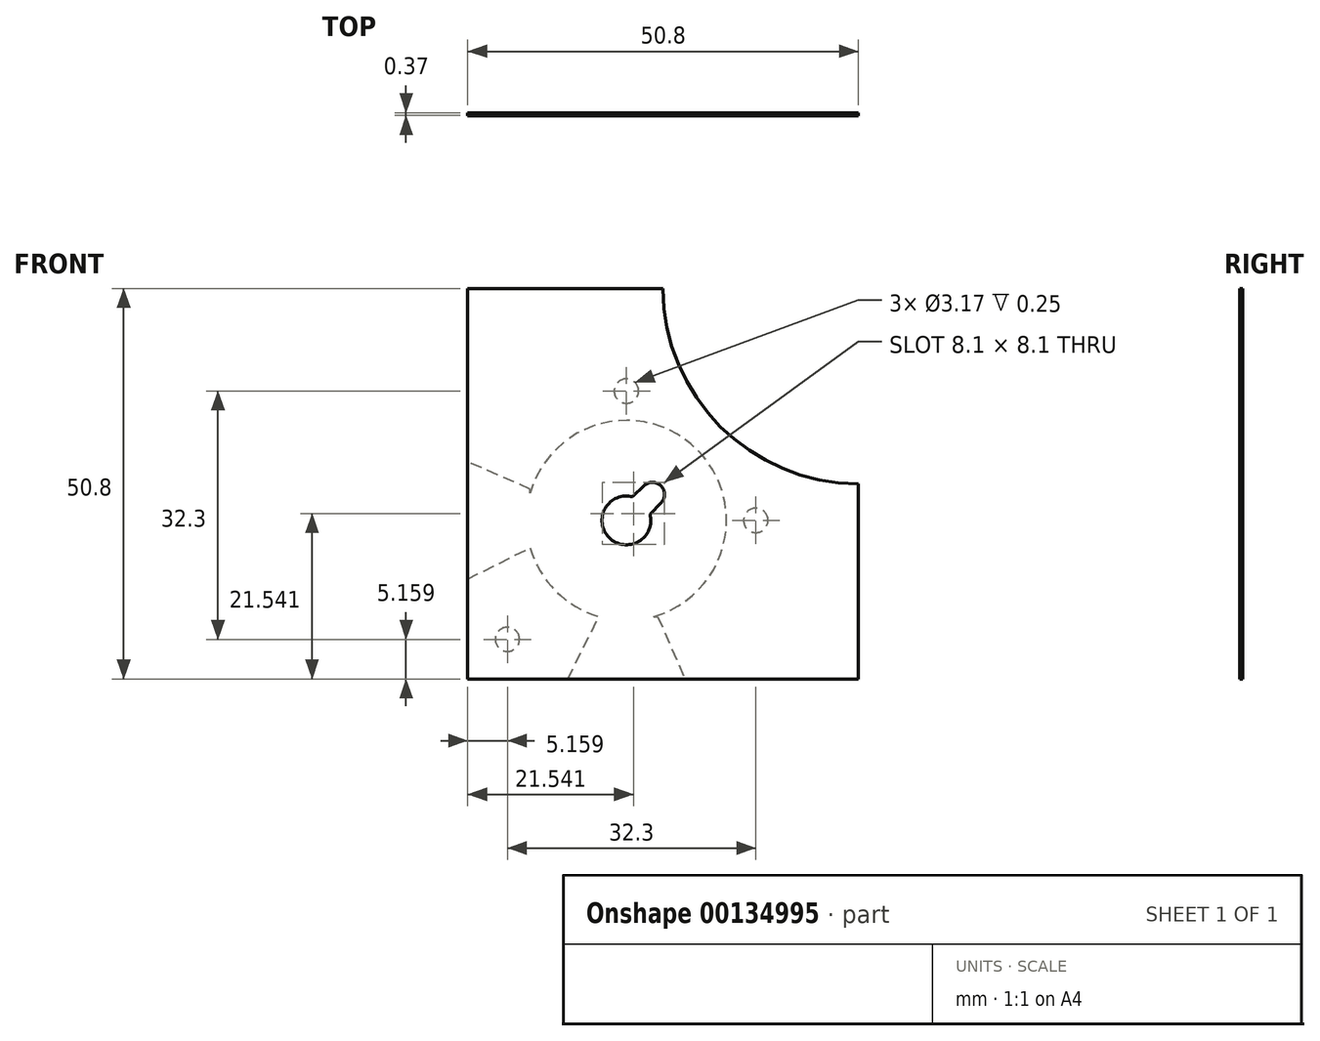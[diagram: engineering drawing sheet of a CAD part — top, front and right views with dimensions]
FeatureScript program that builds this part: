
annotation { "Feature Type Name" : "Feature", "Feature Type Description" : "" }
export const myFeature = defineFeature(function(context is Context, id is Id, definition is map)
    precondition{}
    {
        {
            assignVariable(context, id + "F0", {"name" : "Thickness", "anyValue" : .375});
        }
        {
            var Q0;
            Q0=qCreatedBy(makeId("Front.planeOp"),FACE);
            var sketch = newSketch(context, id + "F1", { "sketchPlane" : qUnion([Q0])});
            skLineSegment(sketch, "E0.bottom", {"start": v(0, 0) * mm, "end": v(50.8, 0) * mm});
            skLineSegment(sketch, "E0.top", {"start": v(0, 50.8) * mm, "end": v(25.4, 50.8) * mm});
            skLineSegment(sketch, "E0.left", {"start": v(0, 0) * mm, "end": v(0, 50.8) * mm});
            skLineSegment(sketch, "E0.right", {"start": v(50.8, 0) * mm, "end": v(50.8, 25.4) * mm});
            skPoint(sketch, "E1.orphan", {"position": v(50.8, 50.8) * mm});
            skArc(sketch, "E2", {"start": v(25.4, 50.8) * mm, "mid": v(32.84, 32.84) * mm, "end": v(50.8, 25.4) * mm});
            skSolve(sketch);
        }
        {
            var Q0;
            Q0=qCreatedBy(makeId("Front.planeOp"),FACE);
            var sketch = newSketch(context, id + "F2", { "sketchPlane" : qUnion([Q0])});
            skCircle(sketch, "E3", {"center": v(10.32, 10.32) * mm, "radius": 3.18 * mm});
            skCircle(sketch, "E4.0.1.0", {"center": v(10.32, 30.96) * mm, "radius": 3.18 * mm});
            skCircle(sketch, "E4.1.0.0", {"center": v(30.96, 10.32) * mm, "radius": 3.18 * mm});
            skLineSegment(sketch, "E4.direction1", {"start": v(10.32, 10.32) * mm, "end": v(30.96, 10.32) * mm, "construction": true});
            skLineSegment(sketch, "E4.direction2", {"start": v(10.32, 10.32) * mm, "end": v(10.32, 30.96) * mm, "construction": true});
            skSolve(sketch);
        }
        {
            var Q0;
            Q0=qCreatedBy(makeId("Front.planeOp"),FACE);
            var sketch = newSketch(context, id + "F3", { "sketchPlane" : qUnion([Q0])});
            skCircle(sketch, "E5", {"center": v(20.64, 20.64) * mm, "radius": 13 * mm});
            skSolve(sketch);
        }
        {
            var Q0;
            Q0=qCreatedBy(makeId("Front.planeOp"),FACE);
            var sketch = newSketch(context, id + "F4", { "sketchPlane" : qUnion([Q0])});
            skCircle(sketch, "E6", {"center": v(20.64, 3.82) * mm, "radius": 1.59 * mm, "construction": true});
            skLineSegment(sketch, "E7", {"start": v(20.64, 0) * mm, "end": v(20.64, 7.63) * mm, "construction": true});
            skLineSegment(sketch, "E8", {"start": v(0, 0) * mm, "end": v(10.32, 10.32) * mm, "construction": true});
            skLineSegment(sketch, "E9", {"start": v(10.32, 30.96) * mm, "end": v(30.96, 10.32) * mm, "construction": true});
            skCircle(sketch, "E10.MirrorC", {"center": v(37.46, 20.64) * mm, "radius": 1.59 * mm});
            skCircle(sketch, "E11.MirrorC", {"center": v(3.82, 20.64) * mm, "radius": 1.59 * mm, "construction": true});
            skCircle(sketch, "E12.MirrorC", {"center": v(20.64, 37.46) * mm, "radius": 1.59 * mm});
            skCircle(sketch, "E13", {"center": v(5.16, 5.16) * mm, "radius": 1.59 * mm});
            skSolve(sketch);
        }
        {
            var Q0;
            Q0=qCreatedBy(makeId("Front.planeOp"),FACE);
            var sketch = newSketch(context, id + "F5", { "sketchPlane" : qUnion([Q0])});
            skCircle(sketch, "E14", {"center": v(15.48, 15.48) * mm, "radius": 1.65 * mm});
            skLineSegment(sketch, "E15", {"start": v(10.32, 10.32) * mm, "end": v(20.64, 20.64) * mm, "construction": true});
            skSolve(sketch);
        }
        {
            var Q0;
            Q0=makeQuery(id+"F1.imprint","IMPRINT",FACE,{"disambiguationData":[TD([[makeQuery(id+"F1.imprint","IMPRINT",EDGE,{"derivedFrom":sQuery(id+"F1.wireOp",EDGE,"E0.bottom")}),1.0]])]});
            var sketch = newSketch(context, id + "F6", { "sketchPlane" : qUnion([Q0])});
            skLineSegment(sketch, "E16", {"start": v(20.64, 20.64) * mm, "end": v(33.64, 20.64) * mm, "construction": true});
            skLineSegment(sketch, "E17", {"start": v(27.14, 20.64) * mm, "end": v(16.82, 0) * mm, "construction": true});
            skLineSegment(sketch, "E18", {"start": v(20.64, 0) * mm, "end": v(13, 0) * mm, "construction": true});
            skLineSegment(sketch, "E19", {"start": v(13, 0) * mm, "end": v(23.32, 20.64) * mm, "construction": true});
            skLineSegment(sketch, "E20", {"start": v(20.64, 0) * mm, "end": v(30.96, 20.64) * mm, "construction": true});
            skLineSegment(sketch, "E21", {"start": v(13, 0) * mm, "end": v(17.07, 8.13) * mm});
            skLineSegment(sketch, "E22", {"start": v(17.07, 8.13) * mm, "end": v(24.7, 8.13) * mm});
            skLineSegment(sketch, "E23", {"start": v(24.7, 8.13) * mm, "end": v(28.27, 0) * mm});
            skLineSegment(sketch, "E24", {"start": v(28.27, 0) * mm, "end": v(13, 0) * mm});
            skLineSegment(sketch, "E25.MirrorCS", {"start": v(0, 28.27) * mm, "end": v(0, 13) * mm});
            skLineSegment(sketch, "E26.MirrorCS", {"start": v(0, 20.64) * mm, "end": v(0, 13) * mm, "construction": true});
            skLineSegment(sketch, "E27.MirrorCS", {"start": v(0, 13) * mm, "end": v(8.13, 17.07) * mm});
            skLineSegment(sketch, "E28.MirrorCS", {"start": v(8.13, 17.07) * mm, "end": v(8.13, 24.7) * mm});
            skLineSegment(sketch, "E29.MirrorCS", {"start": v(8.13, 24.7) * mm, "end": v(0, 28.27) * mm});
            skSolve(sketch);
        }
        {
            var Q0;
            Q0=qCreatedBy(makeId("Front.planeOp"),FACE);
            var sketch = newSketch(context, id + "F7", { "sketchPlane" : qUnion([Q0])});
            skCircle(sketch, "E30", {"center": v(20.64, 20.64) * mm, "radius": 3.18 * mm});
            skSolve(sketch);
        }
        {
            var Q0;
            Q0=qCreatedBy(makeId("Front.planeOp"),FACE);
            var sketch = newSketch(context, id + "F8", { "sketchPlane" : qUnion([Q0])});
            skLineSegment(sketch, "E31", {"start": v(20.64, 20.64) * mm, "end": v(25.13, 25.13) * mm, "construction": true});
            skPoint(sketch, "E32", {"position": v(22.88, 22.88) * mm});
            skLineSegment(sketch, "E33.bottom", {"start": v(21.46, 23.7) * mm, "end": v(22.88, 25.13) * mm});
            skLineSegment(sketch, "E33.top", {"start": v(23.7, 21.46) * mm, "end": v(25.13, 22.88) * mm});
            skLineSegment(sketch, "E33.left", {"start": v(21.46, 23.7) * mm, "end": v(23.7, 21.46) * mm});
            skArc(sketch, "E34", {"start": v(25.13, 22.88) * mm, "mid": v(25.13, 25.13) * mm, "end": v(22.88, 25.13) * mm});
            skSolve(sketch);
        }
        {
            var Q0;
            Q0=makeQuery(id+"F1.imprint","IMPRINT",FACE,{"disambiguationData":[TD([[makeQuery(id+"F1.imprint","IMPRINT",EDGE,{"derivedFrom":sQuery(id+"F1.wireOp",EDGE,"E0.bottom")}),1.0]])]});
            extrude(context, id + "F9", {"entities" : qUnion([Q0]), "depth" : (getVariable(context, 'Thickness') / 3) * mm, "hasSecondDirection" : true, "secondDirectionOppositeDirection" : true, "secondDirectionDepth" : (getVariable(context, 'Thickness') * 2 / 3) * mm});
        }
        {
            var Q0;
            Q0 = qSketchRegion(id + "F8", true);
            var Q1;
            Q1 = qSketchRegion(id + "F7", true);
            extrude(context, id + "F10", {"entities" : qUnion([Q0, Q1]), "operationType" : NewBodyOperationType.REMOVE, "endBound" : BoundingType.THROUGH_ALL, "depth" : 25.4 * mm});
        }
        {
            var Q0;
            Q0 = qSketchRegion(id + "F3", true);
            var Q1;
            Q1 = qSketchRegion(id + "F4", true);
            var Q2;
            Q2 = qSketchRegion(id + "F6", true);
            extrude(context, id + "F11", {"entities" : qUnion([Q0, Q1, Q2]), "operationType" : NewBodyOperationType.REMOVE, "endBound" : BoundingType.THROUGH_ALL, "oppositeDirection" : true, "depth" : 25.4 * mm});
        }
    });
